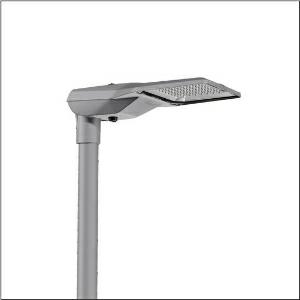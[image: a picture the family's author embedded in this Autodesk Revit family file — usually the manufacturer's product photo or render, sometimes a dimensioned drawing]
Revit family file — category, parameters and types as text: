
# Revit family: streetlight_sl_21_midi___stw1_0a_5xe3e33t08mb_6392
name_source: partatom
category: Lighting Fixtures
units: mm (PartAtom-declared; Revit-internal decimal feet)

## family parameters
Cut with Voids When Loaded = No
Host = Face
Light Source = No
Part Type = Normal
Room Calculation Point = No
Round Connector Dimension = Use Diameter
Shared = No

## types (1)
- --- (1 x LED, 18270 lm, 136 W, 3000K)
    Apparent Load = 136 VA
    CIE Flux Codes = 38 75 98 100 100
    Color Rendering = 70
    Color Temperature = 3000K
    Default Elevation = 1800 mm
    Description = Streetlight SL 21 midi, mast luminaire, primary light control with lens, of PMMA, primary optical cover: cover, of toughened safety glass, transparent, light distribution: STW1.0a, light emission: direct distribution, primary light characteristic: asymmetric, installation type: side-entry, post-top, LED, High Power LED, rated luminous flux: 18.270lm, luminous efficacy: 134lm/W, light colour: 730, colour temperature: 3000K, control gear: D4i, control: overheat protection, constant luminous flux control, time-dependent luminous flux control, flexible luminous flux parameterisation, pre-setting: logarithmic dimming characteristic, mains connection: 230..240V, AC, 50/60Hz, start of lifetime: 136W, end of service life: 142W, reduction: 61W, luminaire housing, of diecast aluminium, powder-coated, Siteco® metallic grey (DB 702S), corrosivity category C5 mid according to DIN EN ISO 12944, please order mast flange separately, inclination adjustable: 0°, 5°, 10°, 15°, sealing non-destructively replaceable, multi-level sealing system, length: 644mm, width: 335mm, height: 110mm, mast flange for spigot size: 42mm (side-entry): 5XC10008XM4, 60/48mm (side-entry/post-top): 5XC10108XM2, 76/60mm (side-entry/post-top): 5XC10108XM1, mounting height: 4..8m, Smart Interface below and above, protection rating (complete): IP66, insulation class (complete): insulation class II (safety insulation), certification: CE, ENEC, ENEC+, VDE, impact resistance: IK10, permissible operating ambient temperature for outdoor applications: -40..+50°C, standard-compliant lighting for roads and squares, packaging unit: 1 piece

Light Distribution: STW1.0a
    Height = 111 mm
    Lamp = 1 x LED
    Lamp Light Flux = 18270 lm
    Lamp Power = 136 W
    Lamp count = 1
    Length = 644 mm
    Luminous efficacy = 134 lm/W
    Manufacturer = Siteco
    ModVariant = No
    Model = 5XE3E33T08MB
    Number of Poles = 1
    OnlyDefault = Yes
    Power Factor = 1
    Product Name = Streetlight SL 21 midi | STW1.0a
    Product group = mast luminaire | pylon top
    ProductGroupID = 6100
    Protection Class = Protection class II
    Protection Degree = IP 66
    RLX_Detail_Level = 1
    RLX_Emergency_Light_Flux = 0 lm
    RLX_Emergency_Type = 0
    RLX_Emergency_Type_DB = No
    RlxData = <blob elided: 27069 chars, md5=9e964f84>
    Socket = socket
    Standby Power = 0 W
    System Light Flux = 18270 lm
    System Power = 136 W
    Type Comments = factory setting: luminous flux: 100 % | dim-lin: 254 | 695 mA
    Type Image = l_1004304.jpg
    URL = http://relux.com
    VarID = @adj_187908
    Voltage = 0 V
    Weight = 0.00 kg
    Width = 336 mm

## geometry (parser evidence)
native form markers: Blend x4, Sweep x12
no freeform markers — native parametric forms only
